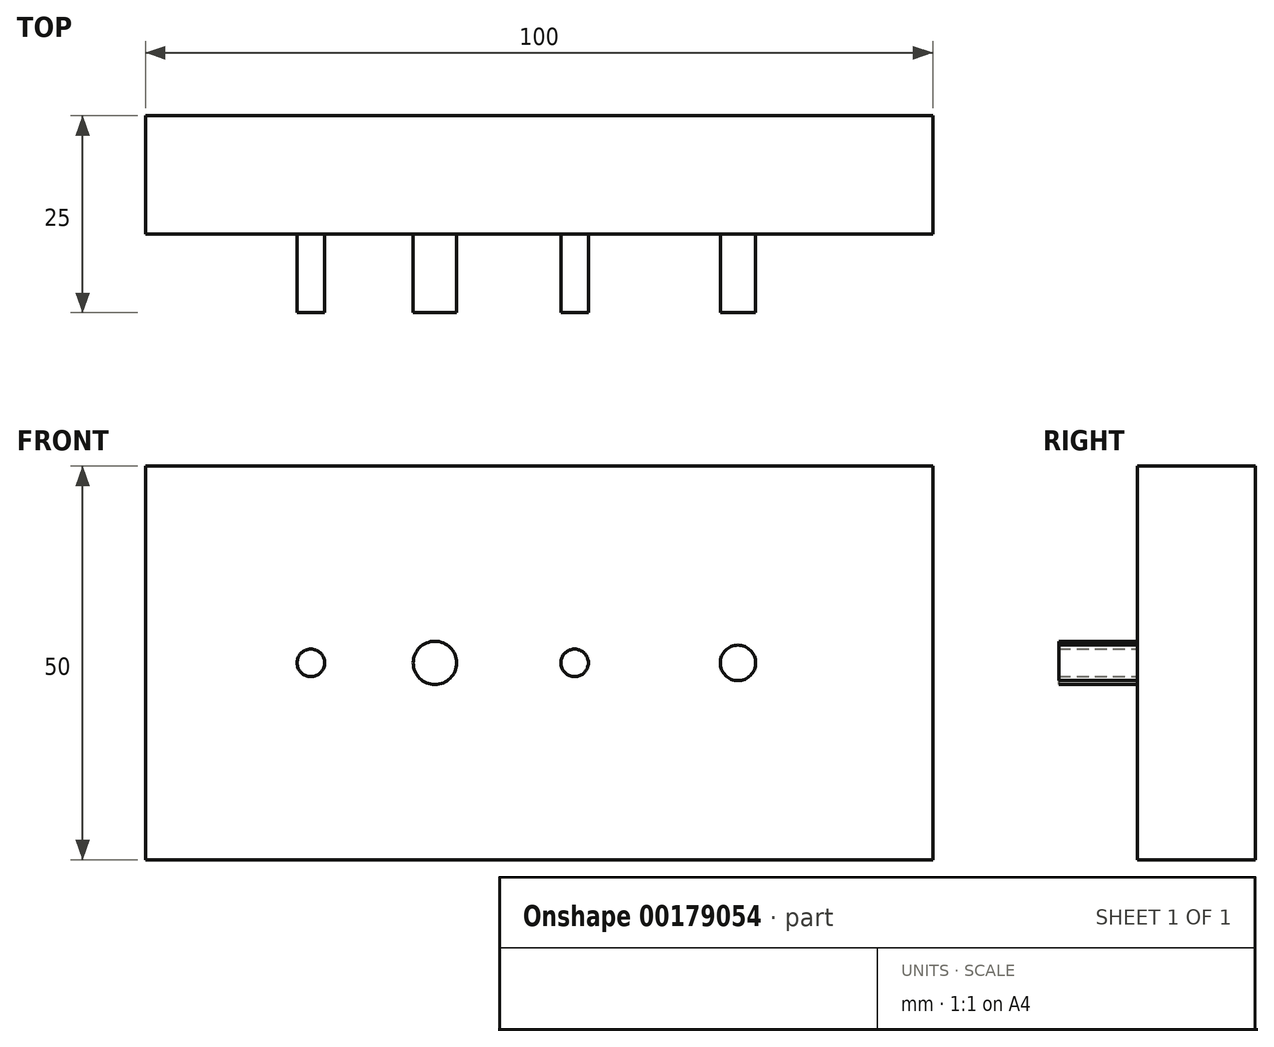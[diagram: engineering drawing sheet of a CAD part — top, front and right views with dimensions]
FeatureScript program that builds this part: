
annotation { "Feature Type Name" : "Feature", "Feature Type Description" : "" }
export const myFeature = defineFeature(function(context is Context, id is Id, definition is map)
    precondition{}
    {
        {
            var Q0;
            Q0=qCreatedBy(makeId("Front.planeOp"),FACE);
            var sketch = newSketch(context, id + "F0", { "sketchPlane" : qUnion([Q0])});
            skLineSegment(sketch, "E0.bottom", {"start": v(50, 25) * mm, "end": v(-50, 25) * mm});
            skLineSegment(sketch, "E0.top", {"start": v(50, -25) * mm, "end": v(-50, -25) * mm});
            skLineSegment(sketch, "E0.left", {"start": v(50, 25) * mm, "end": v(50, -25) * mm});
            skLineSegment(sketch, "E0.right", {"start": v(-50, 25) * mm, "end": v(-50, -25) * mm});
            skPoint(sketch, "E0.middle", {"position": v(0, 0) * mm});
            skSolve(sketch);
        }
        {
            var Q0;
            Q0 = qSketchRegion(id + "F0", true);
            extrude(context, id + "F1", {"entities" : qUnion([Q0]), "depth" : 15 * mm});
        }
        {
            var Q0;
            Q0=makeQuery(id+"F1.opExtrude","CAP_FACE",FACE,{"disambiguationData":[OSD([sQuery(id+"F0.wireOp",EDGE,"E0.bottom"),sQuery(id+"F0.wireOp",EDGE,"E0.top"),sQuery(id+"F0.wireOp",EDGE,"E0.left"),sQuery(id+"F0.wireOp",EDGE,"E0.right")])],"isStart":false});
            var sketch = newSketch(context, id + "F2", { "sketchPlane" : qUnion([Q0])});
            skCircle(sketch, "E1", {"center": v(-29, 0) * mm, "radius": 1.75 * mm});
            skPoint(sketch, "E1.centerSnap0", {"position": v(-50, 0) * mm});
            skSolve(sketch);
        }
        {
            var Q0;
            Q0=makeQuery(id+"F2.imprint","IMPRINT",FACE,{"disambiguationData":[TD([[makeQuery(id+"F2.imprint","IMPRINT",EDGE,{"derivedFrom":sQuery(id+"F2.wireOp",EDGE,"E1")}),1.0]])]});
            extrude(context, id + "F3", {"entities" : qUnion([Q0]), "operationType" : NewBodyOperationType.ADD, "depth" : 10 * mm});
        }
        {
            var Q0;
            Q0=makeQuery(id+"F1.opExtrude","CAP_FACE",FACE,{"disambiguationData":[OSD([sQuery(id+"F0.wireOp",EDGE,"E0.bottom"),sQuery(id+"F0.wireOp",EDGE,"E0.top"),sQuery(id+"F0.wireOp",EDGE,"E0.left"),sQuery(id+"F0.wireOp",EDGE,"E0.right")])],"isStart":false});
            var sketch = newSketch(context, id + "F4", { "sketchPlane" : qUnion([Q0])});
            skCircle(sketch, "E2", {"center": v(-13.25, 0) * mm, "radius": 2.75 * mm});
            skSolve(sketch);
        }
        {
            var Q0;
            Q0 = qSketchRegion(id + "F4", true);
            extrude(context, id + "F5", {"entities" : qUnion([Q0]), "operationType" : NewBodyOperationType.ADD, "depth" : 10 * mm});
        }
        {
            var Q0;
            Q0=makeQuery(id+"F1.opExtrude","CAP_FACE",FACE,{"disambiguationData":[OSD([sQuery(id+"F0.wireOp",EDGE,"E0.bottom"),sQuery(id+"F0.wireOp",EDGE,"E0.top"),sQuery(id+"F0.wireOp",EDGE,"E0.left"),sQuery(id+"F0.wireOp",EDGE,"E0.right")])],"isStart":false});
            var sketch = newSketch(context, id + "F6", { "sketchPlane" : qUnion([Q0])});
            skCircle(sketch, "E3", {"center": v(4.5, 0) * mm, "radius": 1.75 * mm});
            skSolve(sketch);
        }
        {
            var Q0;
            Q0 = qSketchRegion(id + "F6", true);
            extrude(context, id + "F7", {"entities" : qUnion([Q0]), "operationType" : NewBodyOperationType.ADD, "depth" : 10 * mm});
        }
        {
            var Q0;
            Q0=makeQuery(id+"F1.opExtrude","CAP_FACE",FACE,{"disambiguationData":[OSD([sQuery(id+"F0.wireOp",EDGE,"E0.bottom"),sQuery(id+"F0.wireOp",EDGE,"E0.top"),sQuery(id+"F0.wireOp",EDGE,"E0.left"),sQuery(id+"F0.wireOp",EDGE,"E0.right")])],"isStart":false});
            var sketch = newSketch(context, id + "F8", { "sketchPlane" : qUnion([Q0])});
            skCircle(sketch, "E4", {"center": v(25.25, 0) * mm, "radius": 2.25 * mm});
            skSolve(sketch);
        }
        {
            var Q0;
            Q0 = qSketchRegion(id + "F8", true);
            extrude(context, id + "F9", {"entities" : qUnion([Q0]), "operationType" : NewBodyOperationType.ADD, "depth" : 10 * mm});
        }
    });
